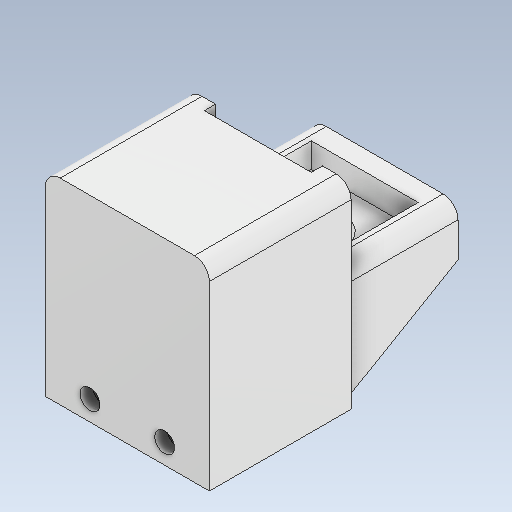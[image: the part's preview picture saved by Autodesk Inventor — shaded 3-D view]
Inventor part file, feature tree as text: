
AUTODESK INVENTOR PART (.ipt)
format: ipt  version: 2020 (Build 240168000, 168)  size: 325,632 bytes
history: native  units: mm
features: extrude x10, sketch x6, other x2, mirror x1, fillet x1, projected_geometry x1
ambient origin geometry x8: Origin, YZ Plane, XZ Plane, XY Plane, X Axis, Y Axis, Z Axis, Center Point
bodies: Body1 (feature_tree)
feature tree (21):
  extrude  "Wyciągnięcie proste8"  Depth=20.5mm
  sketch  "Szkic8"
  other  "Płaszczyzna konstrukcyjna1"
  extrude  "Wyciągnięcie proste9"  Depth=20.5mm
  extrude  "Wyciągnięcie proste14"  Depth=20.5mm
  mirror  "Odbij1"
  extrude  "Wyciągnięcie proste10"  Depth=20.5mm
  extrude  "Wyciągnięcie proste11"  Depth=50.0mm
  extrude  "Wyciągnięcie proste12"  Depth=25.0mm
  extrude  "Wyciągnięcie proste13"  Depth=8.0mm
  sketch  "Szkic12"
  extrude  "Wyciągnięcie proste17"  Depth=8.0mm
  extrude  "Wyciągnięcie proste15"  Depth=8.0mm
  extrude  "Wyciągnięcie proste16"  Depth=75.0mm TaperAngle=0.0deg
  fillet  "Zaokrąglenie1"  Radius=22.0mm
  other  "Pogrubienie1"
  sketch  "Szkic7"
  sketch  "Szkic9"
  sketch  "Szkic10"
  sketch  "Szkic13"
  projected_geometry  "Pętla rzutowana1"
